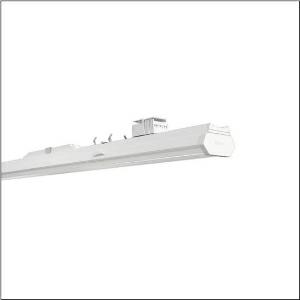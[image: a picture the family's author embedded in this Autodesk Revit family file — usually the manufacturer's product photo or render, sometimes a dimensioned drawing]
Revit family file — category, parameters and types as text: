
# Revit family: licross_r__11_protected_ho_51ts11vn4dxrd_eb6c
name_source: partatom
category: Lighting Fixtures
units: mm (PartAtom-declared; Revit-internal decimal feet)

## family parameters
Cut with Voids When Loaded = No
Host = Face
Light Source = No
Part Type = Normal
Room Calculation Point = No
Round Connector Dimension = Use Diameter
Shared = No

## types (1)
- --- (1 x LED, 2060 lm, 13.5 W, 4000K)
    Apparent Load = 14 VA
    CIE Flux Codes = 84 94 98 99 100
    Color Rendering = 80
    Color Temperature = 4000K
    Default Elevation = 1800 mm
    Description = Licross® 11 Protected HO, luminaire insert, of sheet steel, galvanised, coil coated, white, length: 1.500mm, width: 90mm, height: 101mm, LED rated luminous flux: 13.190lm, light colour: 840, control gear: DALI 2, CLO, control gear: ECG DALI, with plug, 6-pole, with phase selection, mains connection: 220..240V, AC/DC, 0/50..60Hz, halogen-free wiring, for central battery installations according to DIN EN 60598-2-22, for emergency light function, without changeover relay, primary optical cover: cover, of PMMA, light emission: direct with ceiling illumination distribution, protection rating (complete): IP50, insulation class (complete): insulation class I (protective earthing), certification: CE, ENEC, VDE, UKCA, protection symbol: D if used in an environment with non-conductive dust loads with corresponding accessories, permissible ambient temperature for indoor applications: -25..+35°C, standard: EN 60598-2-22, corresponds to IFS (International Featured Standards) requirements for safety and quality in the food industry, reducing of maximum allowable ambient temperature of 5°C with ceiling mounting, LABS conformity tested according to VDMA 24364:2018-05, packaging unit: 1 piece
    Height = 92 mm
    Lamp = 1 x LED
    Lamp Light Flux = 2060 lm
    Lamp Power = 13.5 W
    Lamp count = 1
    Length = 1500 mm
    Luminous efficacy = 153 lm/W
    Manufacturer = Siteco
    ModVariant = No
    Model = 51TS11VN4DXRD
    Mounting Place = Ceiling
    Mounting Type = Pendant
    Number of Poles = 1
    OnlyDefault = Yes
    Power Factor = 1
    Product Name = Licross® 11 Protected HO
    Product group = luminaire insert
    ProductGroupID = 902
    Protection Class = Protection class I
    Protection Degree = IP 50
    RLX_Detail_Level = 1
    RlxData = <blob elided: 24829 chars, md5=9fd31ca8>
    Socket = socket
    Standby Power = 0 W
    System Light Flux = 2060 lm
    System Power = 14 W
    Type Comments = : DC mode (central or group accumulator) initial emergency light level
    Type Image = l_1256145.jpg
    URL = http://relux.com
    VarID = @adj_120885
    Voltage = 0 V
    Weight = 0.00 kg
    Width = 88 mm

## geometry (parser evidence)
native form markers: Blend x4, Sweep x10
no freeform markers — native parametric forms only
